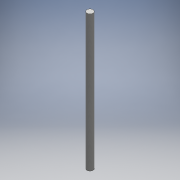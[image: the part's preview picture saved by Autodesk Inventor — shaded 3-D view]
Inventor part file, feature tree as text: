
AUTODESK INVENTOR PART (.ipt)
format: ipt  version: 2018 (Build 220112000, 112)  size: 94,720 bytes
history: native  units: mm
features: other x1, extrude x1, thread x1, sketch x1
ambient origin geometry x8: Origin, YZ Plane, XZ Plane, XY Plane, X Axis, Y Axis, Z Axis, Center Point
bodies: Body1 (feature_tree)
feature tree (4):
  other  "ソリッド1"
  extrude  "押し出し1"  Depth=10.0mm
  thread  "ねじ1"
  sketch  "スケッチ1"
